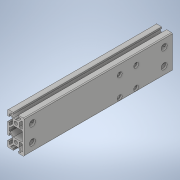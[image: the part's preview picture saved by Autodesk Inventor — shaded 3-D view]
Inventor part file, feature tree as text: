
AUTODESK INVENTOR PART (.ipt)
format: ipt  version: 2022 (Build 260153000, 153)  size: 506,368 bytes
history: native  units: mm
features: sketch x9, hole x8, other x7, extrude x1, pattern_linear x1
ambient origin geometry x8: Origin, YZ Plane, XZ Plane, XY Plane, X Axis, Y Axis, Z Axis, Center Point
bodies: Solid1 (feature_tree)
feature tree (26):
  extrude  "Extrusion1"  Depth=10.0mm TaperAngle=0.0deg
  hole  "Hole1"  [1 undecoded]
  pattern_linear  "Rectangular Pattern1"  Spacing1=3.0mm  [1 undecoded]
  hole  "Hole2"  [1 undecoded]
  hole  "Hole3"  [1 undecoded]
  hole  "Hole6"  [1 undecoded]
  hole  "Hole7"  [1 undecoded]
  other  "C1_XY"
  other  "C1_YZ"
  other  "C1_ZX"
  other  "C1_X"
  other  "C1_Y"
  other  "C1_Z"
  other  "C1_Center"
  sketch  "スケッチ10"
  hole  "穴10"  [1 undecoded]
  hole  "穴12"  [1 undecoded]
  hole  "穴13"  [1 undecoded]
  sketch  "Sketch_63"  dims[d50=7.35mm d51=6.0mm d52=4.0mm d53=2.0mm d54=90.0deg d55=20.0mm d56=0.0mm d64=0.0mm d65=3.0mm d66=136.0mm d67=20.0mm d69=20.0mm d70=20.0mm d72=24.0mm d86=3.5mm d87=6.0mm d88=6.0mm d89=2.0mm d90=90.0deg d91=4.0mm d92=20.594885mm d100=10.0mm d101=3.0mm d102=20.0mm d103=10.0mm d104=170.0mm d105=9.0mm d106=6.0mm d107=4.0mm d108=2.0mm d109=90.0deg d110=6.0mm d111=20.594885mm d112=6.0mm d113=6.0mm d114=4.0mm d115=2.0mm d116=90.0deg d117=5.5mm d118=20.594885mm]
  sketch  "Sketch2"  dims[d0=180.0mm d1=0.0mm]
  sketch  "Sketch3"  dims[d2=4.2mm d3=6.0mm d4=4.0mm d5=2.0mm d6=90.0deg d7=180.0mm d8=0.0mm d9=20.0mm d11=20.0mm d12=10.0mm d14=0.0mm]
  sketch  "Sketch4"  dims[d15=7.35mm d16=6.0mm d17=4.0mm d18=2.0mm d19=90.0deg d20=20.0mm d21=0.0mm]
  sketch  "Sketch7"  dims[d22=7.35mm d23=6.0mm d24=4.0mm d25=2.0mm d26=90.0deg d27=20.0mm d28=0.0mm]
  sketch  "Sketch8"  dims[d43=7.35mm d44=6.0mm d45=4.0mm d46=2.0mm d47=90.0deg d48=20.0mm d49=0.0mm]
  sketch  "スケッチ12"
  sketch  "スケッチ13"
note: 9 required parameter values undecoded (feature->parameter linkage not recoverable at this tier; creation-order binding heuristic only, values carry confidence <= 0.55)
